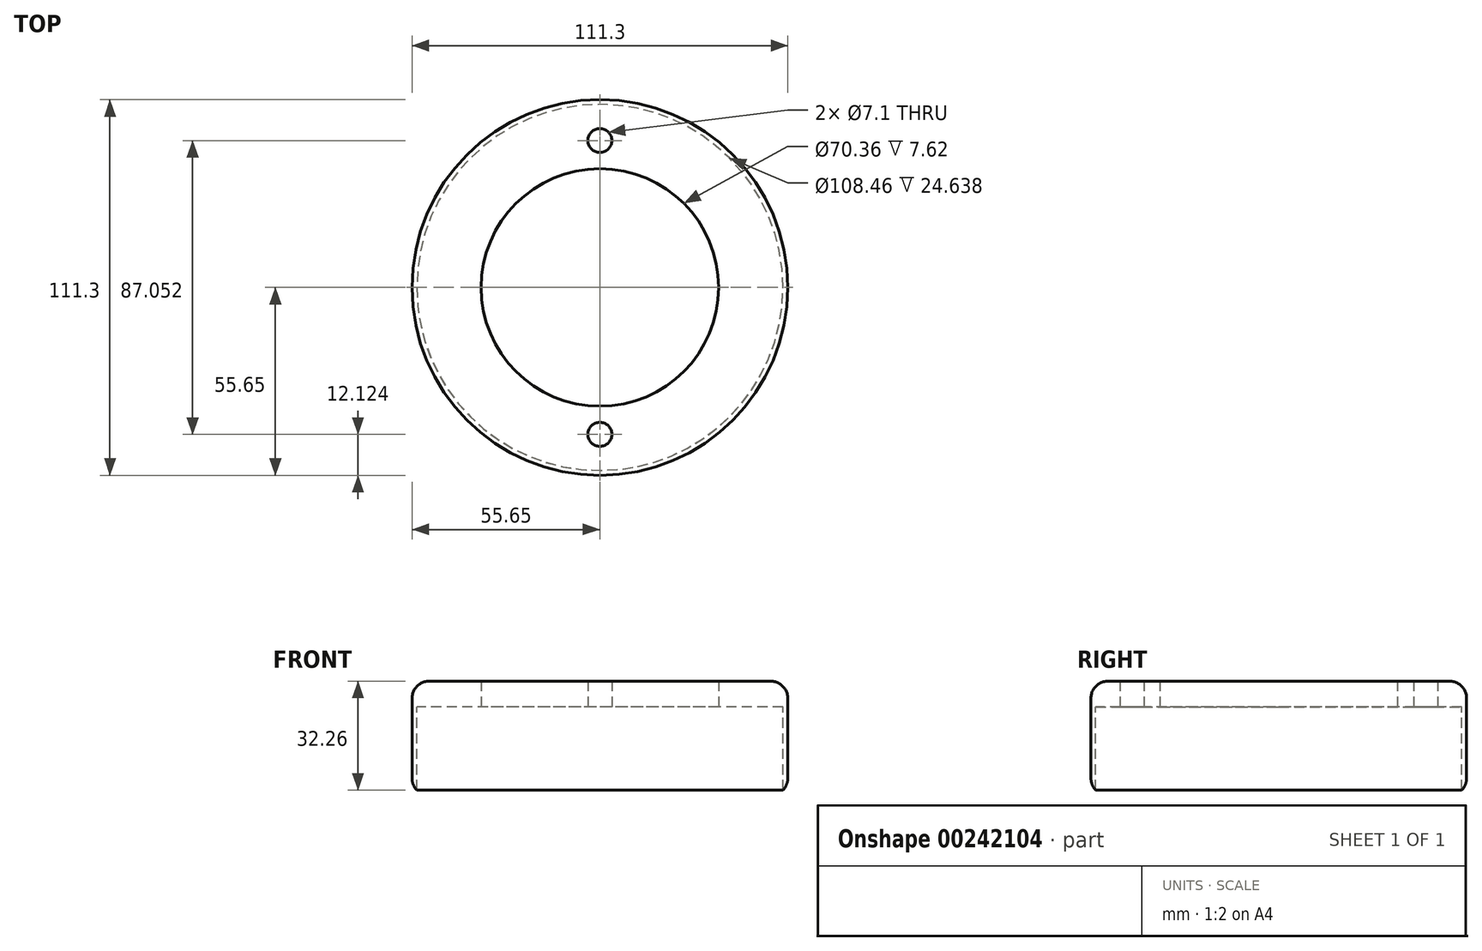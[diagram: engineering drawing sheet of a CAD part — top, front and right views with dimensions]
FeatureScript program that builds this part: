
annotation { "Feature Type Name" : "Feature", "Feature Type Description" : "" }
export const myFeature = defineFeature(function(context is Context, id is Id, definition is map)
    precondition{}
    {
        {
            var Q0;
            Q0=qCreatedBy(makeId("Top.planeOp"),FACE);
            var sketch = newSketch(context, id + "F0", { "sketchPlane" : qUnion([Q0])});
            skPoint(sketch, "E0.middle", {"position": v(0, 0) * mm});
            skCircle(sketch, "E1", {"center": v(0, 0) * mm, "radius": 35.18 * mm});
            skCircle(sketch, "E2", {"center": v(0, 0) * mm, "radius": 54.23 * mm});
            skCircle(sketch, "E3", {"center": v(0, 0) * mm, "radius": 55.65 * mm});
            skCircle(sketch, "E4", {"center": v(0, 43.53) * mm, "radius": 3.55 * mm});
            skLineSegment(sketch, "E5", {"start": v(-54.23, 0) * mm, "end": v(54.23, 0) * mm});
            skCircle(sketch, "E6.MirrorC", {"center": v(0, -43.53) * mm, "radius": 3.55 * mm});
            skLineSegment(sketch, "E7", {"start": v(0, 55.65) * mm, "end": v(0, -54.23) * mm});
            skSolve(sketch);
        }
        {
            var Q0;
            Q0=makeQuery(id+"F0.imprint","IMPRINT",FACE,{"disambiguationData":[TD([[makeQuery(id+"F0.imprint","IMPRINT",EDGE,{"derivedFrom":sQuery(id+"F0.wireOp",EDGE,"E1")}),-1.0]])]});
            var Q1;
            Q1=makeQuery(id+"F0.imprint","IMPRINT",FACE,{"disambiguationData":[TD([[makeQuery(id+"F0.imprint","IMPRINT",EDGE,{"derivedFrom":sQuery(id+"F0.wireOp",EDGE,"E2")}),-1.0]])]});
            extrude(context, id + "F1", {"entities" : qUnion([Q0, Q1]), "depth" : 7.62 * mm});
        }
        {
            var Q0;
            Q0 = qSketchRegion(id + "F0", true);
            extrude(context, id + "F2", {"entities" : qUnion([Q0]), "operationType" : NewBodyOperationType.ADD, "oppositeDirection" : true, "depth" : 24.64 * mm});
        }
        {
            var Q0;
            Q0=makeQuery(id+"F1.opExtrude","CAP_EDGE",EDGE,{"disambiguationData":[OSD([sQuery(id+"F0.wireOp",EDGE,"E3")])],"isStart":false});
            var Q1;
            Q1=makeQuery(id+"F2.opExtrude","CAP_EDGE",EDGE,{"disambiguationData":[OSD([sQuery(id+"F0.wireOp",EDGE,"E3")])],"isStart":false});
            fillet(context, id + "F3", {"entities" : qUnion([Q0, Q1]), "radius" : 5.08 * mm, "tangentPropagation" : true, "allowEdgeOverflow" : false});
        }
    });
